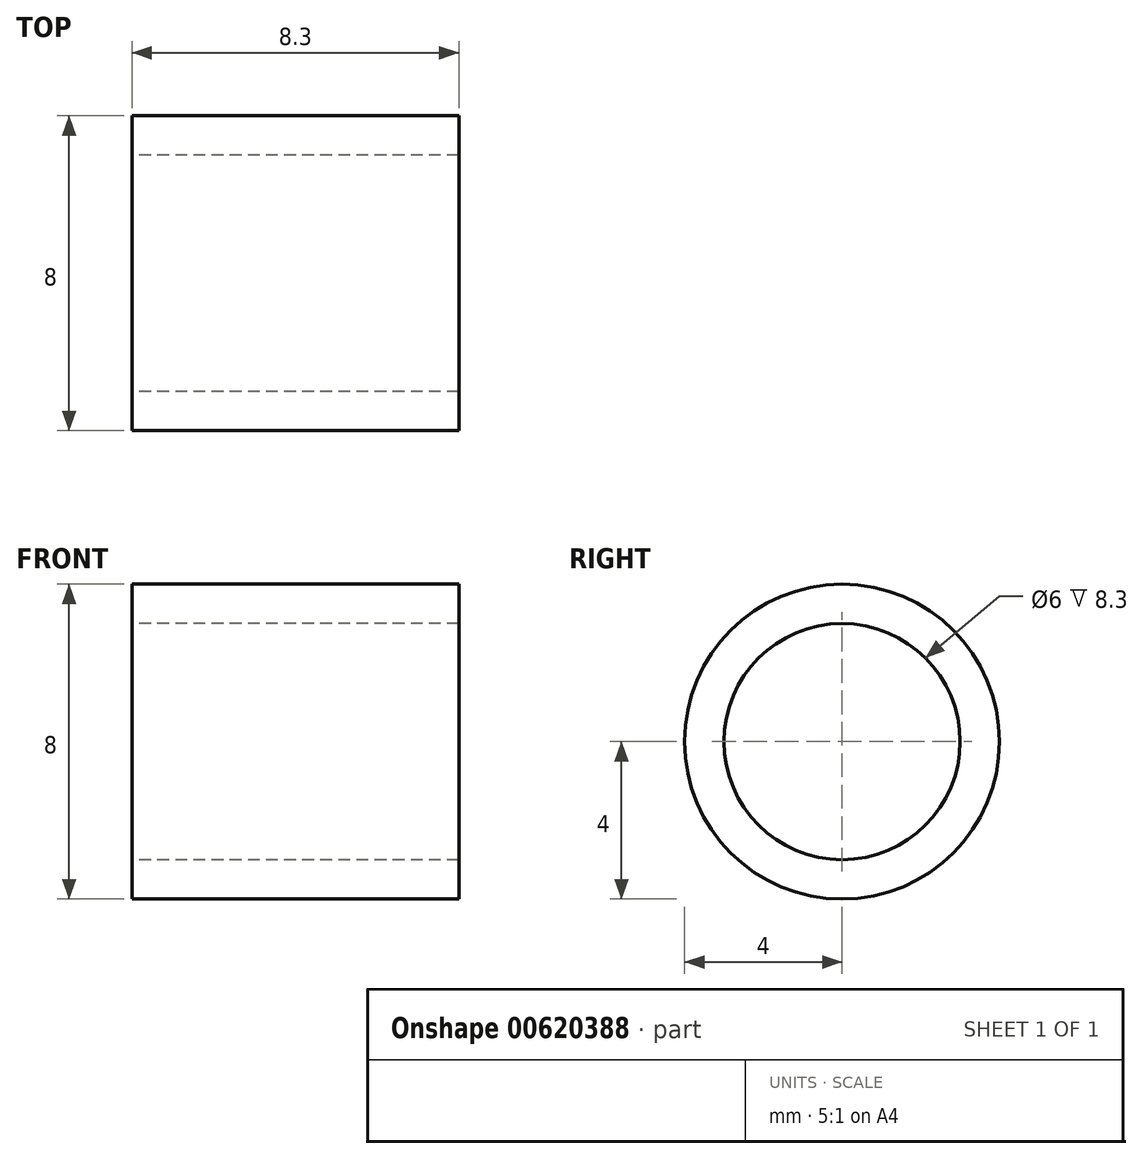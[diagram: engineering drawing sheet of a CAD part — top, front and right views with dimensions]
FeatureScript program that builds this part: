
annotation { "Feature Type Name" : "Feature", "Feature Type Description" : "" }
export const myFeature = defineFeature(function(context is Context, id is Id, definition is map)
    precondition{}
    {
        {
            var Q0;
            Q0=qCreatedBy(makeId("Right.planeOp"),FACE);
            var sketch = newSketch(context, id + "F0", { "sketchPlane" : qUnion([Q0])});
            skCircle(sketch, "E0", {"center": v(0, 0) * mm, "radius": 4 * mm});
            skPoint(sketch, "E1", {"position": v(4, 0) * mm});
            skSolve(sketch);
        }
        {
            var Q0;
            Q0=qSketchRegion(id+"F0",true);
            extrude(context, id + "F1", {"entities" : qUnion([Q0]), "depth" : 8.3 * mm, "offsetDistance" : 25 * mm});
        }
        {
            var Q0;
            Q0=sQuery(id+"F0.wireOp",VERTEX,"E0.center");
            var Q1;
            Q1=makeQuery(id+"F1.opExtrude","SWEPT_BODY",BODY,{"disambiguationData":[OSD([sQuery(id+"F0.wireOp",EDGE,"E0")])]});
            hole(context, id + "F2", {"style" : HoleStyle.SIMPLE, "endStyle" : HoleEndStyle.THROUGH, "oppositeDirection" : true, "holeDiameter" : 6 * mm, "majorDiameter" : 5 * mm, "isTappedThrough" : true, "tappedDepth" : 12 * mm, "tapClearance" : 3, "locations" : qUnion([Q0]), "scope" : qUnion([Q1])});
        }
    });
